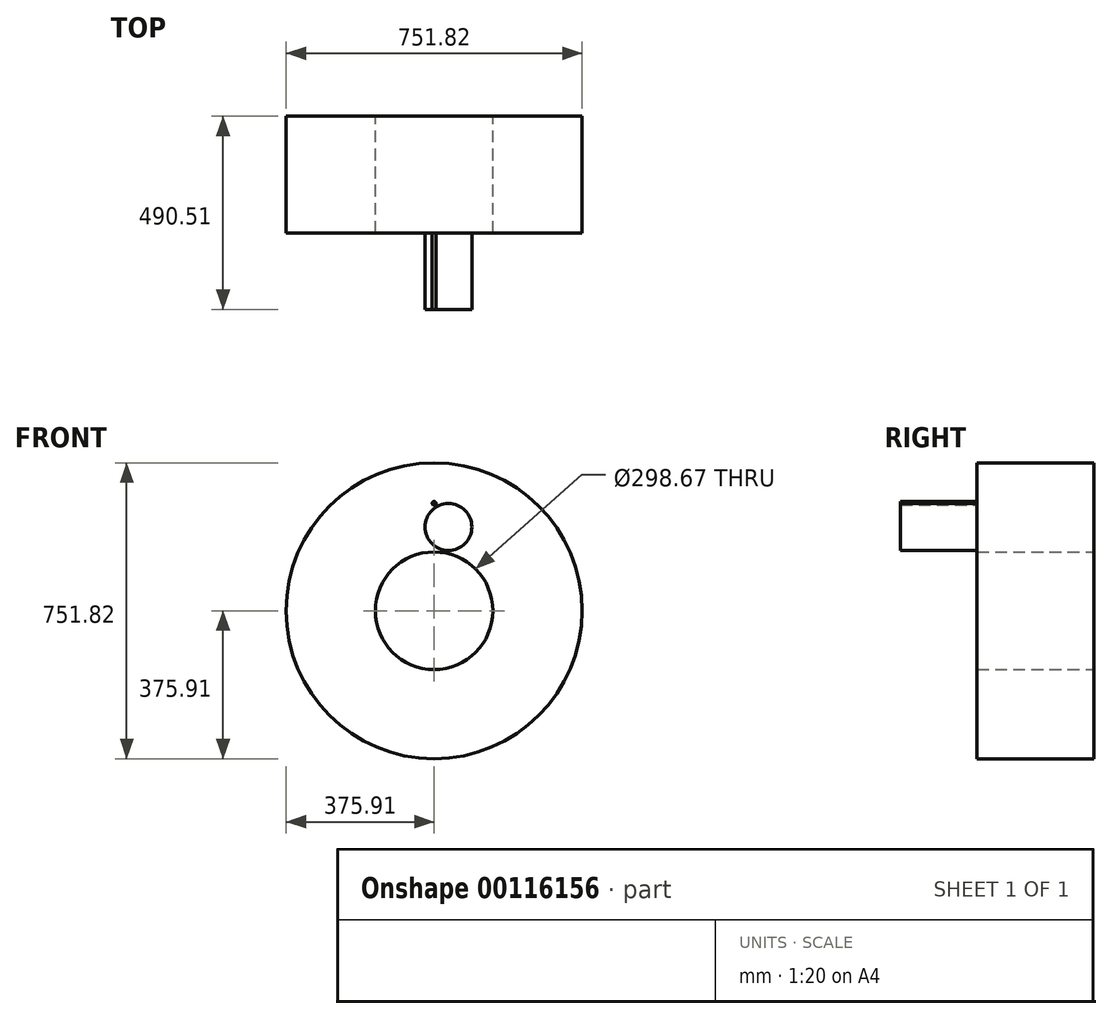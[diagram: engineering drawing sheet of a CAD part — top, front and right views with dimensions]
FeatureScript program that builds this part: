
annotation { "Feature Type Name" : "Feature", "Feature Type Description" : "" }
export const myFeature = defineFeature(function(context is Context, id is Id, definition is map)
    precondition{}
    {
        {
            var Q0;
            Q0=qCreatedBy(makeId("Front.planeOp"),FACE);
            var sketch = newSketch(context, id + "F0", { "sketchPlane" : qUnion([Q0])});
            skCircle(sketch, "E0", {"center": v(0, 0) * mm, "radius": 375.9 * mm});
            skSolve(sketch);
        }
        {
            var Q0;
            Q0 = qSketchRegion(id + "F0", true);
            extrude(context, id + "F1", {"entities" : qUnion([Q0]), "depth" : 270.8 * mm});
        }
        {
            var Q0;
            Q0=qCreatedBy(makeId("Front.planeOp"),FACE);
            var sketch = newSketch(context, id + "F2", { "sketchPlane" : qUnion([Q0])});
            skCircle(sketch, "E1", {"center": v(0, 0) * mm, "radius": 149.34 * mm});
            skCircle(sketch, "E2.0.0", {"center": v(0, 0) * mm, "radius": 375.9 * mm});
            skSolve(sketch);
        }
        {
            var Q0;
            Q0=makeQuery(id+"F2.imprint","IMPRINT",FACE,{"disambiguationData":[TD([[makeQuery(id+"F2.imprint","IMPRINT",EDGE,{"derivedFrom":sQuery(id+"F2.wireOp",EDGE,"E1")}),1.0]])]});
            extrude(context, id + "F3", {"entities" : qUnion([Q0]), "operationType" : NewBodyOperationType.REMOVE, "depth" : 705.4 * mm});
        }
        {
            var Q0;
            Q0=qCreatedBy(makeId("Front.planeOp"),FACE);
            var sketch = newSketch(context, id + "F4", { "sketchPlane" : qUnion([Q0])});
            skCircle(sketch, "E3", {"center": v(0, 272.89) * mm, "radius": 4.75 * mm});
            skCircle(sketch, "E4", {"center": v(36.39, 212.77) * mm, "radius": 59.63 * mm});
            skSolve(sketch);
        }
        {
            var Q0;
            Q0 = qSketchRegion(id + "F4", true);
            extrude(context, id + "F5", {"entities" : qUnion([Q0]), "operationType" : NewBodyOperationType.ADD, "depth" : 465.1 * mm});
        }
        {
            var Q0;
            Q0=qCreatedBy(makeId("Front.planeOp"),FACE);
            var sketch = newSketch(context, id + "F6", { "sketchPlane" : qUnion([Q0])});
            skLineSegment(sketch, "E5", {"start": v(0, 264.98) * mm, "end": v(36.39, 217.52) * mm});
            skLineSegment(sketch, "E6", {"start": v(36.39, 165.32) * mm, "end": v(36.39, 217.52) * mm});
            skLineSegment(sketch, "E7", {"start": v(31.64, 212.77) * mm, "end": v(91.75, 233.34) * mm});
            skSolve(sketch);
        }
        {
            var Q0;
            Q0 = qSketchRegion(id + "F6", true);
            var Q1;
            Q1=makeQuery(id+"F1.opExtrude","CAP_FACE",FACE,{"disambiguationData":[OSD([sQuery(id+"F0.wireOp",EDGE,"E0")])],"isStart":true});
            extrude(context, id + "F7", {"entities" : qUnion([Q0, Q1]), "operationType" : NewBodyOperationType.ADD, "depth" : 25.4 * mm});
        }
    });
